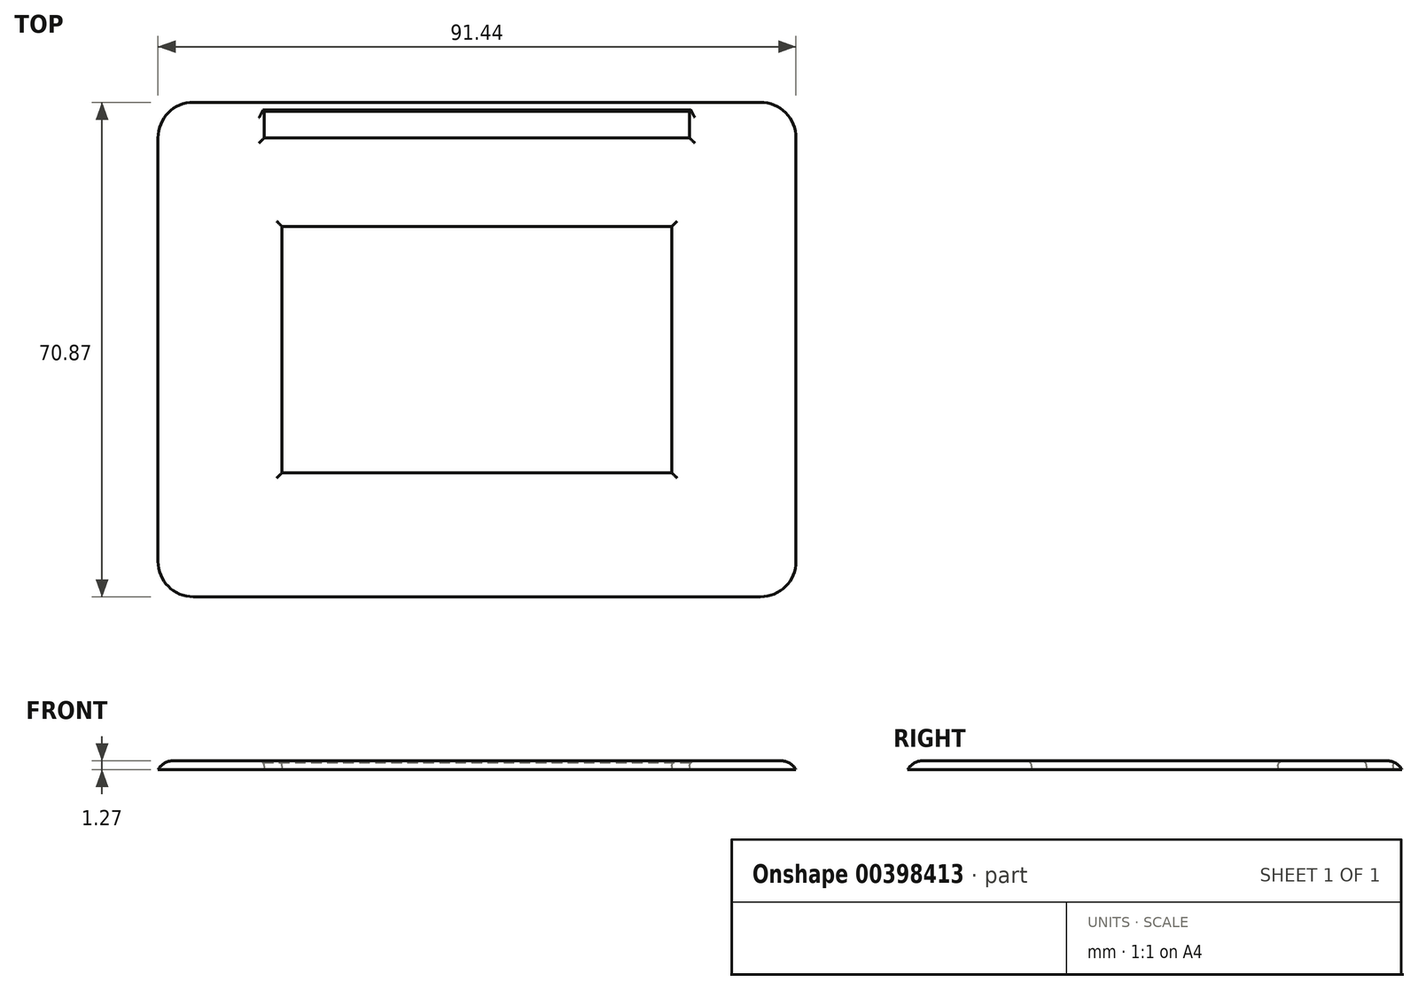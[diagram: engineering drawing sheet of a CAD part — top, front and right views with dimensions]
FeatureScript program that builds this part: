
annotation { "Feature Type Name" : "Feature", "Feature Type Description" : "" }
export const myFeature = defineFeature(function(context is Context, id is Id, definition is map)
    precondition{}
    {
        {
            var Q0;
            Q0=qCreatedBy(makeId("Top.planeOp"),FACE);
            var sketch = newSketch(context, id + "F0", { "sketchPlane" : qUnion([Q0])});
            skLineSegment(sketch, "E0.bottom", {"start": v(0, 0) * mm, "end": v(91.44, 0) * mm});
            skLineSegment(sketch, "E0.top", {"start": v(0, -70.87) * mm, "end": v(91.44, -70.87) * mm});
            skLineSegment(sketch, "E0.left", {"start": v(0, 0) * mm, "end": v(0, -70.87) * mm});
            skLineSegment(sketch, "E0.right", {"start": v(91.44, 0) * mm, "end": v(91.44, -70.87) * mm});
            skLineSegment(sketch, "E1.0", {"start": v(17.78, -17.78) * mm, "end": v(73.66, -17.78) * mm});
            skLineSegment(sketch, "E1.1", {"start": v(17.78, -17.78) * mm, "end": v(17.78, -53.09) * mm});
            skLineSegment(sketch, "E1.2", {"start": v(17.78, -53.09) * mm, "end": v(73.66, -53.09) * mm});
            skLineSegment(sketch, "E1.3", {"start": v(73.66, -17.78) * mm, "end": v(73.66, -53.09) * mm});
            skLineSegment(sketch, "E2", {"start": v(45.72, -1.27) * mm, "end": v(15.24, -1.27) * mm});
            skLineSegment(sketch, "E3", {"start": v(15.24, -1.27) * mm, "end": v(15.24, -5.08) * mm});
            skLineSegment(sketch, "E4", {"start": v(15.24, -5.08) * mm, "end": v(76.2, -5.08) * mm});
            skLineSegment(sketch, "E5", {"start": v(76.2, -5.08) * mm, "end": v(76.2, -1.27) * mm});
            skLineSegment(sketch, "E6", {"start": v(76.2, -1.27) * mm, "end": v(45.72, -1.27) * mm});
            skSolve(sketch);
        }
        {
            var Q0;
            Q0=makeQuery(id+"F0.imprint","IMPRINT",FACE,{"disambiguationData":[TD([[makeQuery(id+"F0.imprint","IMPRINT",EDGE,{"derivedFrom":sQuery(id+"F0.wireOp",EDGE,"E0.bottom")}),-1.0]])]});
            extrude(context, id + "F1", {"entities" : qUnion([Q0]), "depth" : 1.27 * mm});
        }
        {
            var Q0;
            Q0=makeQuery(id+"F1.opExtrude","SWEPT_EDGE",EDGE,{"disambiguationData":[OSD([sQuery(id+"F0.wireOp",EDGE,"E0.top"),sQuery(id+"F0.wireOp",EDGE,"E0.right")])]});
            var Q1;
            Q1=makeQuery(id+"F1.opExtrude","SWEPT_EDGE",EDGE,{"disambiguationData":[OSD([sQuery(id+"F0.wireOp",EDGE,"E0.bottom"),sQuery(id+"F0.wireOp",EDGE,"E0.right")])]});
            var Q2;
            Q2=makeQuery(id+"F1.opExtrude","SWEPT_EDGE",EDGE,{"disambiguationData":[OSD([sQuery(id+"F0.wireOp",EDGE,"E0.bottom"),sQuery(id+"F0.wireOp",EDGE,"E0.left")])]});
            var Q3;
            Q3=makeQuery(id+"F1.opExtrude","SWEPT_EDGE",EDGE,{"disambiguationData":[OSD([sQuery(id+"F0.wireOp",EDGE,"E0.top"),sQuery(id+"F0.wireOp",EDGE,"E0.left")])]});
            fillet(context, id + "F2", {"entities" : qUnion([Q0, Q1, Q2, Q3]), "radius" : 5.08 * mm, "tangentPropagation" : true, "allowEdgeOverflow" : false});
        }
        {
            var Q0;
            Q0=makeQuery(id+"F1.opExtrude","CAP_EDGE",EDGE,{"disambiguationData":[OSD([sQuery(id+"F0.wireOp",EDGE,"E1.1")])],"isStart":false});
            var Q1;
            Q1=makeQuery(id+"F1.opExtrude","CAP_EDGE",EDGE,{"disambiguationData":[OSD([sQuery(id+"F0.wireOp",EDGE,"E1.0")])],"isStart":false});
            var Q2;
            Q2=makeQuery(id+"F1.opExtrude","CAP_EDGE",EDGE,{"disambiguationData":[OSD([sQuery(id+"F0.wireOp",EDGE,"E1.2")])],"isStart":false});
            var Q3;
            Q3=makeQuery(id+"F1.opExtrude","CAP_EDGE",EDGE,{"disambiguationData":[OSD([sQuery(id+"F0.wireOp",EDGE,"E1.3")])],"isStart":false});
            var Q4;
            Q4=makeQuery(id+"F1.opExtrude","CAP_EDGE",EDGE,{"disambiguationData":[OSD([sQuery(id+"F0.wireOp",EDGE,"E4")])],"isStart":false});
            var Q5;
            Q5=makeQuery(id+"F1.opExtrude","CAP_EDGE",EDGE,{"disambiguationData":[OSD([sQuery(id+"F0.wireOp",EDGE,"E5")])],"isStart":false});
            var Q6;
            Q6=makeQuery(id+"F1.opExtrude","CAP_EDGE",EDGE,{"disambiguationData":[OSD([sQuery(id+"F0.wireOp",EDGE,"E2"),sQuery(id+"F0.wireOp",EDGE,"E6")])],"isStart":false});
            var Q7;
            Q7=makeQuery(id+"F1.opExtrude","CAP_EDGE",EDGE,{"disambiguationData":[OSD([sQuery(id+"F0.wireOp",EDGE,"E3")])],"isStart":false});
            fillet(context, id + "F3", {"entities" : qUnion([Q0, Q1, Q2, Q3, Q4, Q5, Q6, Q7]), "radius" : 0.76 * mm, "tangentPropagation" : true, "allowEdgeOverflow" : false});
        }
        {
            var Q0;
            Q0=makeQuery(id+"F1.opExtrude","CAP_EDGE",EDGE,{"disambiguationData":[OSD([sQuery(id+"F0.wireOp",EDGE,"E0.left")])],"isStart":false});
            fillet(context, id + "F4", {"entities" : qUnion([Q0]), "radius" : 2.54 * mm, "tangentPropagation" : true, "allowEdgeOverflow" : false});
        }
    });
